# Revit family: Kälteschelle ALU-PU 80 -s-, DS 20, M10-M12, Ø139,7-168,3
name_source: partatom
category: HLS-Bauteile
revit_build: Autodesk Revit 2017 (Build: 20190507_1515(x64)
units: mm (PartAtom-declared; Revit-internal decimal feet)

## family parameters
Arbeitsebenenbasiert = Ja
Beim Laden mit Abzugskörper schneiden = Nein
Bemaßung runder Anschluss = Durchmesser verwenden
Gemeinsam genutzt = Ja
Immer vertikal = Nein
Raumberechnungspunkt = Nein
Teiletyp = Normal

## types (3) — shared parameters
A = 45 mm
Anschluss = M10/M12
Baustoffklasse = B2
DS = 20 mm  [stored 0.0656168 ft]
DVS = 18 mm
Dichte Kern = 80 kg/m³
Dichte Mantel = 2.700 kg/m³
Dicke Mantel = 0,08 mm
Dämmkörper = ALU/PU
Dämmstärke = 20 mm  [stored 0.0656168 ft]
Fabrikat = MEFA
Firma = MEFA Befestigungs- und Montagesysteme GmbH
HGA = 22 mm  [stored 0.0721785 ft]
Kurztext1 = Kälteschelle RG80s ALU/PU
L = 100 mm  [stored 0.328084 ft]
MB = 30 mm  [stored 0.0984252 ft]
MD = 3 mm  [stored 0.00984252 ft]
Material = Stahl
Material Mantel = Alufolie
Materialname = S235
Mengeneinheit = St
Oberflaeche = galvanisch verzinkt
Rohrschellentyp = Maxima PSM
Schalenlänge = 100 mm
Vorgabe-Ansicht = 1219 mm
Wasserdampfdiffusionswiderstand = 18750 µ
Wärmeleitfähigkeit = 0.025 W/mK
max. Temperaturbeständigkeit = 120 °C
mittl. Nenndruckfestigkeit Kern = 0,5 N/mm²
stat. Belastung Kern = 0,1 N/mm²
vpe = 1 St

## per-type parameters (varying)
| type | AB | Anschlußhöhe | Artikelnummer | B | Breite | D | D0 | DF1 | DF2 | Dmax | Dmin | EAN | Gewicht | Gewicht pro Bauteil | H | Kurztext2 | R | RM | Rohraußendurchmesser Stahl | S | max. zul. Last |
| Kälteschelle ALU-PU 80 -s-, DS 20, M10/M12, Ø139,7 | 2 mm  [stored 0.00656168 ft] | 45 mm | 75614042 | 253 mm | 252 mm | 140 mm | 180 mm | 32 mm  [stored 0.104987 ft] | 33 mm | 142 mm | 138 mm | 4250928443687 | 0.67 kg | 0.67 kg | 208 mm | 139,7 mm Iso 20 x 100 mm M10/M12 | 90 mm | 93 mm | 139,7 mm | 221 mm | 0.80 kN |
| Kälteschelle ALU-PU 80 -s-, DS 20, M10/M12, Ø159 | 1 mm  [stored 0.00328084 ft] | 46 mm | 75615942 | 279 mm  [stored 0.915354 ft] | 278 mm | 159 mm  [stored 0.521654 ft] | 199 mm  [stored 0.652887 ft] | 35 mm  [stored 0.114829 ft] | 36 mm | 162 mm | 158 mm | 4250928443724 | 0.76 kg | 0.76 kg | 227 mm | 159 mm Iso 20 x 100 mm M10/M12 | 100 mm  [stored 0.328084 ft] | 103 mm | 159 mm | 244 mm  [stored 0.800525 ft] | 0.90 kN |
| Kälteschelle ALU-PU 80 -s-, DS 20, M10/M12, Ø168,3 | 0 mm  [stored 0 ft] | 45 mm | 75616842 | 288 mm | 288 mm | 168 mm | 208 mm | 36 mm | 36 mm | 170 mm | 168 mm | 4250928443762 | 0.77 kg | 0.77 kg | 236 mm | 168,3 mm Iso 20 x 100 mm M10/M12 | 104 mm | 107 mm | 168,3 mm | 252 mm | 1.10 kN |

note: [stored X ft] marks values corroborated as IEEE doubles in the binary element streams (Revit-internal decimal feet)

## geometry (parser evidence)
native form markers: Sweep x6
no freeform markers — native parametric forms only
